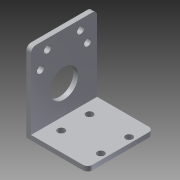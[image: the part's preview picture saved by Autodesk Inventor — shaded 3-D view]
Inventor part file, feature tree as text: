
AUTODESK INVENTOR PART (.ipt)
format: ipt  version: 2013 (Build 170138000, 138)  size: 143,360 bytes
history: native  units: in
note: dims shown in document units (in); Inventor stores cm internally (conversion verified against a paired STEP export)
features: extrude x3, sketch x3, fillet x1
ambient origin geometry x8: Origin, YZ Plane, XZ Plane, XY Plane, X Axis, Y Axis, Z Axis, Center Point
bodies: Solid1 (feature_tree)
feature tree (7):
  extrude  "Extrusion1"  Depth=2.5in
  extrude  "Extrusion2"  Depth=1.75in TaperAngle=0.0deg
  extrude  "Extrusion3"  Depth=0.625in
  fillet  "Fillet1"  Radius=0.1875in
  sketch  "Sketch1"  dims[d0=2.0in d1=2.5in]
  sketch  "Sketch2"  dims[d2=0.125in d3=1.75in d4=0.0in]
  sketch  "Sketch3"  dims[d5=0.875in d6=0.625in d7=0.1875in d8=0.1875in d9=1.5in d10=0.0in d11=0.75in d12=0.875in d13=0.75in d17=0.1875in d18=0.425in d19=1.0in d20=0.0in d21=1.625in d22=0.7874in d24=1.05in d25=0.3937in d27=1.0in d29=0.125in d30=0.375in d31=0.625in d32=1.25in]
